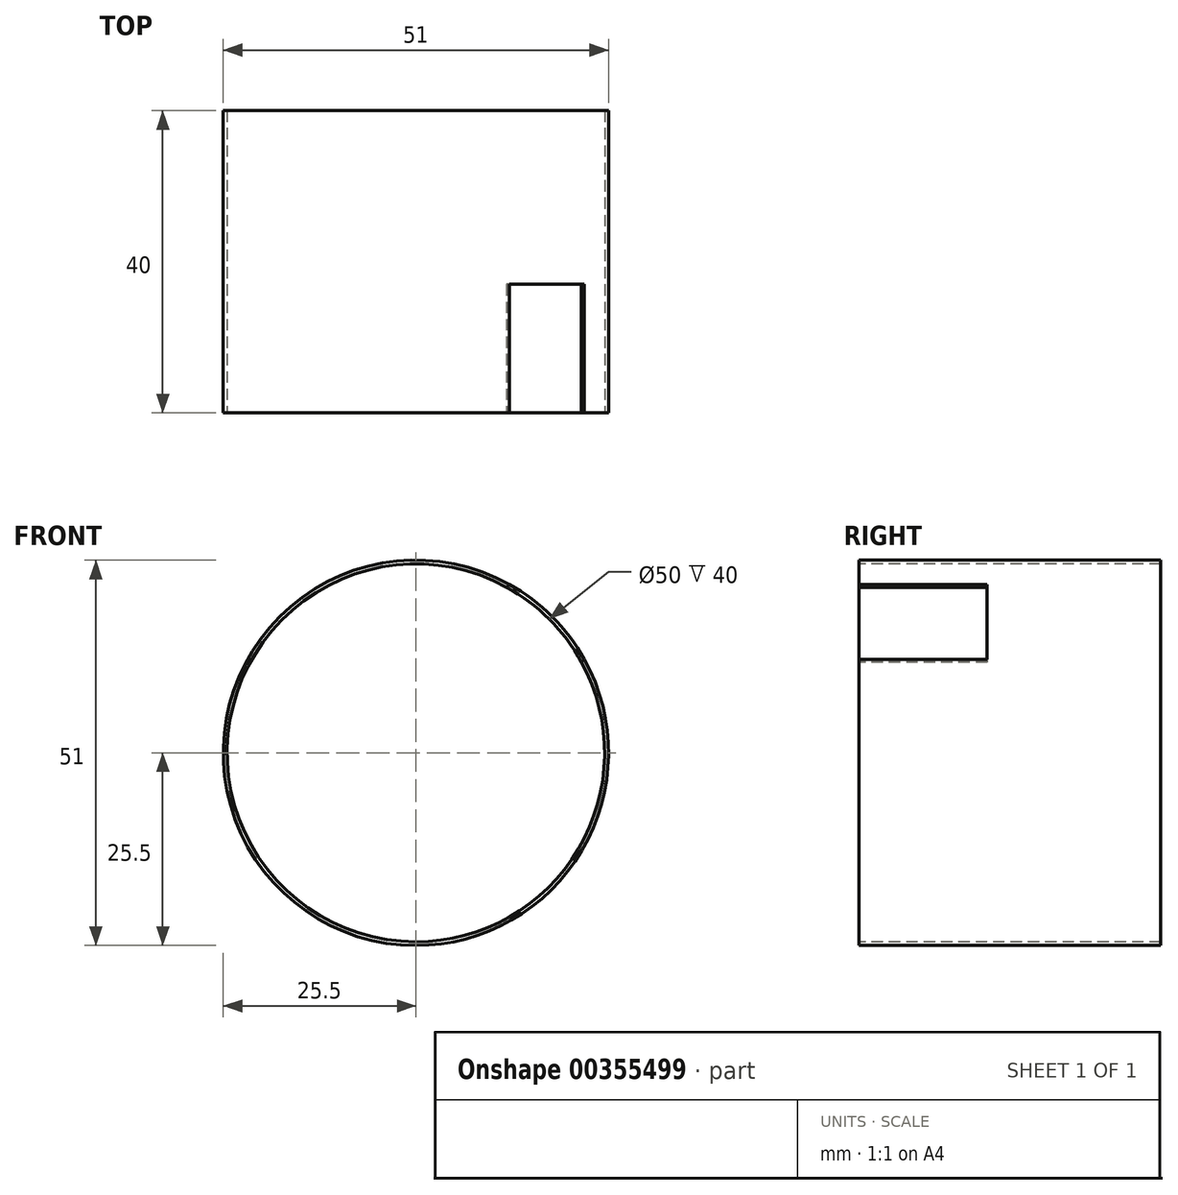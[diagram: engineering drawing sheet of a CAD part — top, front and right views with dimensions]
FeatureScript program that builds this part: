
annotation { "Feature Type Name" : "Feature", "Feature Type Description" : "" }
export const myFeature = defineFeature(function(context is Context, id is Id, definition is map)
    precondition{}
    {
        {
            var Q0;
            Q0=qCreatedBy(makeId("Front.planeOp"),FACE);
            var sketch = newSketch(context, id + "F0", { "sketchPlane" : qUnion([Q0])});
            skCircle(sketch, "E0", {"center": v(0, 0) * mm, "radius": 25 * mm});
            skCircle(sketch, "E1", {"center": v(0, 0) * mm, "radius": 25.5 * mm});
            skLineSegment(sketch, "E2", {"start": v(12.39, 22.29) * mm, "end": v(12.02, 21.92) * mm});
            skLineSegment(sketch, "E3.MirrorCS", {"start": v(22.29, 12.39) * mm, "end": v(21.92, 12.02) * mm});
            skPoint(sketch, "E4.start.orphan", {"position": v(0, 25.5) * mm});
            skPoint(sketch, "E5.start.orphan", {"position": v(25.5, 0) * mm});
            skPoint(sketch, "E6.start.orphan", {"position": v(18.03, 18.03) * mm});
            skSolve(sketch);
        }
        {
            var Q0;
            {var subQ0=sQuery(id+"F0.wireOp",EDGE,"E2");Q0=makeQuery(id+"F0.imprint","IMPRINT",FACE,{"disambiguationData":[TD([[makeQuery(id+"F0.imprint","IMPRINT",EDGE,{"derivedFrom":subQ0}),-1.0]])]});}
            extrude(context, id + "F1", {"entities" : qUnion([Q0]), "oppositeDirection" : true, "depth" : 40 * mm});
        }
        {
            var Q0;
            {var subQ0=sQuery(id+"F0.wireOp",EDGE,"E2");Q0=makeQuery(id+"F0.imprint","IMPRINT",FACE,{"disambiguationData":[TD([[makeQuery(id+"F0.imprint","IMPRINT",EDGE,{"derivedFrom":subQ0}),1.0]])]});}
            extrude(context, id + "F2", {"entities" : qUnion([Q0]), "operationType" : NewBodyOperationType.ADD, "oppositeDirection" : true, "depth" : 40 * mm});
        }
        {
            var Q0;
            {var subQ0=sQuery(id+"F0.wireOp",EDGE,"E2");Q0=makeQuery(id+"F0.imprint","IMPRINT",FACE,{"disambiguationData":[TD([[makeQuery(id+"F0.imprint","IMPRINT",EDGE,{"derivedFrom":subQ0}),1.0]])]});}
            extrude(context, id + "F3", {"entities" : qUnion([Q0]), "operationType" : NewBodyOperationType.REMOVE, "oppositeDirection" : true, "depth" : 17 * mm});
        }
    });
